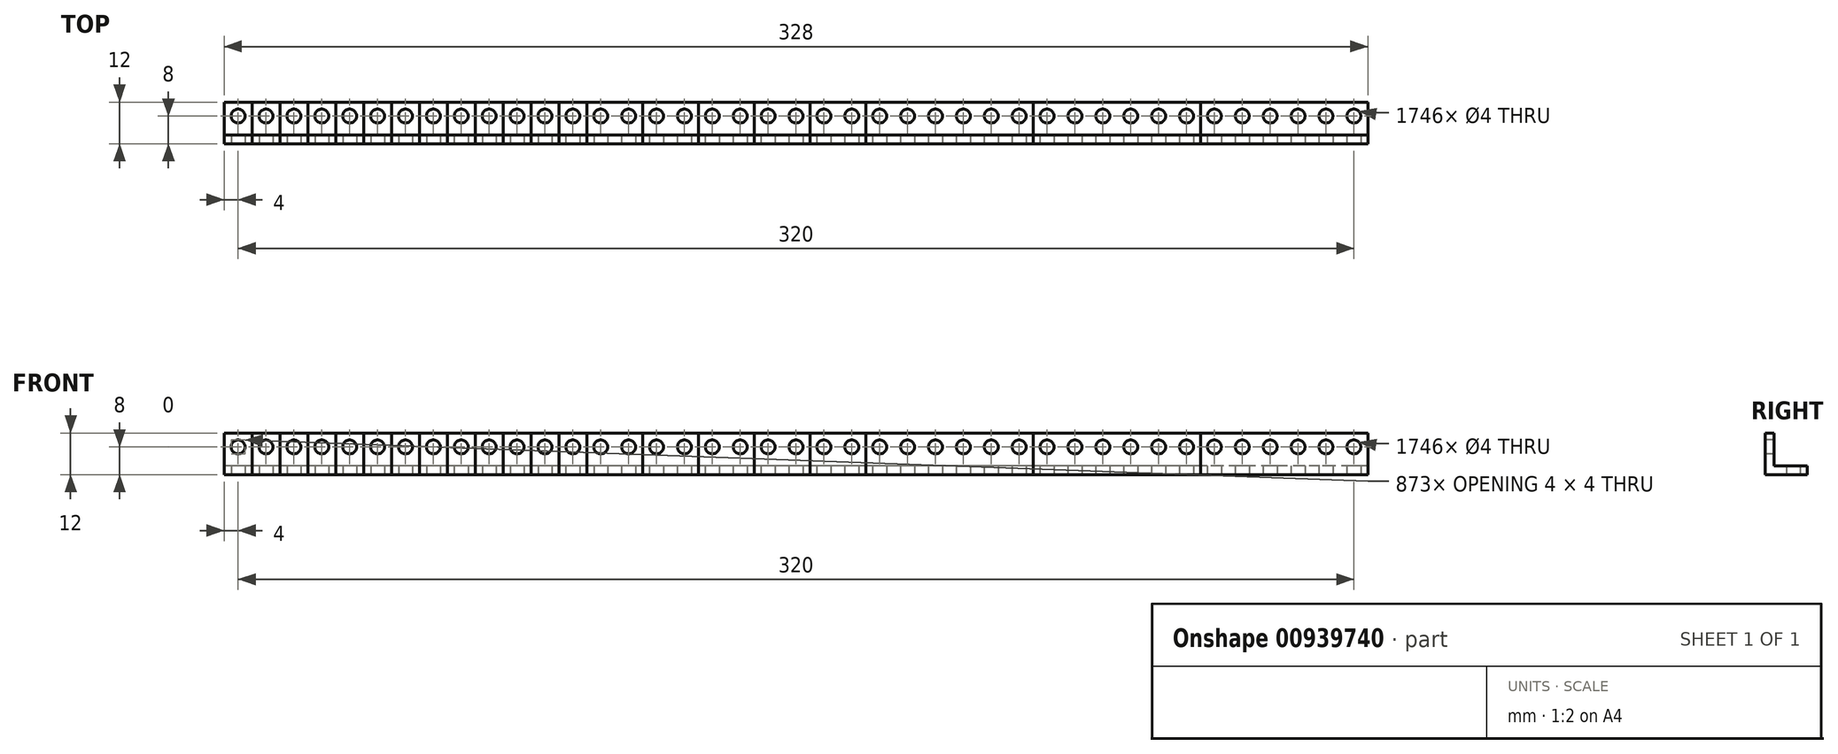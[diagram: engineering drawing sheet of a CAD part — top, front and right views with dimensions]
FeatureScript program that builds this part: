
annotation { "Feature Type Name" : "Feature", "Feature Type Description" : "" }
export const myFeature = defineFeature(function(context is Context, id is Id, definition is map)
    precondition{}
    {
        {
            var Q0;
            Q0=qCreatedBy(makeId("Right.planeOp"),FACE);
            var sketch = newSketch(context, id + "F0", { "sketchPlane" : qUnion([Q0])});
            skLineSegment(sketch, "E0.bottom", {"start": v(0, 0) * mm, "end": v(12, 0) * mm});
            skLineSegment(sketch, "E0.top", {"start": v(0, 12) * mm, "end": v(2.5, 12) * mm});
            skLineSegment(sketch, "E0.left", {"start": v(0, 0) * mm, "end": v(0, 12) * mm});
            skLineSegment(sketch, "E1.left", {"start": v(2.5, 12) * mm, "end": v(2.5, 2.5) * mm});
            skLineSegment(sketch, "E2", {"start": v(12, 0) * mm, "end": v(12, 2.5) * mm});
            skLineSegment(sketch, "E3", {"start": v(2.5, 2.5) * mm, "end": v(12, 2.5) * mm});
            skSolve(sketch);
        }
        {
            var Q0;
            Q0=qSketchRegion(id+"F0",true);
            extrude(context, id + "F1", {"entities" : qUnion([Q0]), "depth" : 8 * mm, "offsetDistance" : 25 * mm});
        }
        {
            var Q0;
            Q0=qSketchRegion(id+"F0",true);
            extrude(context, id + "F2", {"entities" : qUnion([Q0]), "depth" : 16 * mm, "offsetDistance" : 25 * mm});
        }
        {
            var Q0;
            Q0=qSketchRegion(id+"F0",true);
            extrude(context, id + "F3", {"entities" : qUnion([Q0]), "depth" : 24 * mm, "offsetDistance" : 25 * mm});
        }
        {
            var Q0;
            Q0=qSketchRegion(id+"F0",true);
            extrude(context, id + "F4", {"entities" : qUnion([Q0]), "depth" : 32 * mm, "offsetDistance" : 25 * mm});
        }
        {
            var Q0;
            Q0=qSketchRegion(id+"F0",true);
            extrude(context, id + "F5", {"entities" : qUnion([Q0]), "depth" : 40 * mm, "offsetDistance" : 25 * mm});
        }
        {
            var Q0;
            Q0=qSketchRegion(id+"F0",true);
            extrude(context, id + "F6", {"entities" : qUnion([Q0]), "depth" : 48 * mm, "offsetDistance" : 25 * mm});
        }
        {
            var Q0;
            Q0=qSketchRegion(id+"F0",true);
            extrude(context, id + "F7", {"entities" : qUnion([Q0]), "depth" : 56 * mm, "offsetDistance" : 25 * mm});
        }
        {
            var Q0;
            Q0=qSketchRegion(id+"F0",true);
            extrude(context, id + "F8", {"entities" : qUnion([Q0]), "depth" : 64 * mm, "offsetDistance" : 25 * mm});
        }
        {
            var Q0;
            Q0=qSketchRegion(id+"F0",true);
            extrude(context, id + "F9", {"entities" : qUnion([Q0]), "depth" : 72 * mm, "offsetDistance" : 25 * mm});
        }
        {
            var Q0;
            Q0=qSketchRegion(id+"F0",true);
            extrude(context, id + "F10", {"entities" : qUnion([Q0]), "depth" : 80 * mm, "offsetDistance" : 25 * mm});
        }
        {
            var Q0;
            Q0=qSketchRegion(id+"F0",true);
            extrude(context, id + "F11", {"entities" : qUnion([Q0]), "depth" : 88 * mm, "offsetDistance" : 25 * mm});
        }
        {
            var Q0;
            Q0=qSketchRegion(id+"F0",true);
            extrude(context, id + "F12", {"entities" : qUnion([Q0]), "depth" : 96 * mm, "offsetDistance" : 25 * mm});
        }
        {
            var Q0;
            Q0=qSketchRegion(id+"F0",true);
            extrude(context, id + "F13", {"entities" : qUnion([Q0]), "depth" : 104 * mm, "offsetDistance" : 25 * mm});
        }
        {
            var Q0;
            Q0=qSketchRegion(id+"F0",true);
            extrude(context, id + "F14", {"entities" : qUnion([Q0]), "depth" : 120 * mm, "offsetDistance" : 25 * mm});
        }
        {
            var Q0;
            Q0=qSketchRegion(id+"F0",true);
            extrude(context, id + "F15", {"entities" : qUnion([Q0]), "depth" : 136 * mm, "offsetDistance" : 25 * mm});
        }
        {
            var Q0;
            Q0=qSketchRegion(id+"F0",true);
            extrude(context, id + "F16", {"entities" : qUnion([Q0]), "depth" : 152 * mm, "offsetDistance" : 25 * mm});
        }
        {
            var Q0;
            Q0=qSketchRegion(id+"F0",true);
            extrude(context, id + "F17", {"entities" : qUnion([Q0]), "depth" : 168 * mm, "offsetDistance" : 25 * mm});
        }
        {
            var Q0;
            Q0=qSketchRegion(id+"F0",true);
            extrude(context, id + "F18", {"entities" : qUnion([Q0]), "depth" : 184 * mm, "offsetDistance" : 25 * mm});
        }
        {
            var Q0;
            Q0=qSketchRegion(id+"F0",true);
            extrude(context, id + "F19", {"entities" : qUnion([Q0]), "depth" : 232 * mm, "offsetDistance" : 25 * mm});
        }
        {
            var Q0;
            Q0=qSketchRegion(id+"F0",true);
            extrude(context, id + "F20", {"entities" : qUnion([Q0]), "depth" : 280 * mm, "offsetDistance" : 25 * mm});
        }
        {
            var Q0;
            Q0=qSketchRegion(id+"F0",true);
            extrude(context, id + "F21", {"entities" : qUnion([Q0]), "depth" : 328 * mm, "offsetDistance" : 25 * mm});
        }
        {
            var Q0;
            Q0=qCreatedBy(makeId("Front.planeOp"),FACE);
            var sketch = newSketch(context, id + "F22", { "sketchPlane" : qUnion([Q0])});
            skLineSegment(sketch, "E4.bottom", {"start": v(0, 0) * mm, "end": v(4, 0) * mm, "construction": true});
            skLineSegment(sketch, "E4.top", {"start": v(0, 8) * mm, "end": v(4, 8) * mm, "construction": true});
            skLineSegment(sketch, "E4.left", {"start": v(0, 0) * mm, "end": v(0, 8) * mm, "construction": true});
            skLineSegment(sketch, "E4.right", {"start": v(4, 0) * mm, "end": v(4, 8) * mm, "construction": true});
            skCircle(sketch, "E5", {"center": v(4, 8) * mm, "radius": 2 * mm});
            skCircle(sketch, "E6.1.0.0", {"center": v(12, 8) * mm, "radius": 2 * mm});
            skCircle(sketch, "E6.2.0.0", {"center": v(20, 8) * mm, "radius": 2 * mm});
            skLineSegment(sketch, "E6.direction1", {"start": v(4, 8) * mm, "end": v(12, 8) * mm, "construction": true});
            skCircle(sketch, "E7.0.3.0", {"center": v(28, 8) * mm, "radius": 2 * mm});
            skCircle(sketch, "E7.0.4.0", {"center": v(36, 8) * mm, "radius": 2 * mm});
            skCircle(sketch, "E7.0.5.0", {"center": v(44, 8) * mm, "radius": 2 * mm});
            skCircle(sketch, "E7.0.6.0", {"center": v(52, 8) * mm, "radius": 2 * mm});
            skCircle(sketch, "E7.0.7.0", {"center": v(60, 8) * mm, "radius": 2 * mm});
            skCircle(sketch, "E7.0.8.0", {"center": v(68, 8) * mm, "radius": 2 * mm});
            skCircle(sketch, "E7.0.9.0", {"center": v(76, 8) * mm, "radius": 2 * mm});
            skCircle(sketch, "E7.0.10.0", {"center": v(84, 8) * mm, "radius": 2 * mm});
            skCircle(sketch, "E7.0.11.0", {"center": v(92, 8) * mm, "radius": 2 * mm});
            skCircle(sketch, "E7.0.12.0", {"center": v(100, 8) * mm, "radius": 2 * mm});
            skCircle(sketch, "E7.0.13.0", {"center": v(108, 8) * mm, "radius": 2 * mm});
            skCircle(sketch, "E7.0.14.0", {"center": v(116, 8) * mm, "radius": 2 * mm});
            skCircle(sketch, "E7.0.15.0", {"center": v(124, 8) * mm, "radius": 2 * mm});
            skCircle(sketch, "E7.0.16.0", {"center": v(132, 8) * mm, "radius": 2 * mm});
            skCircle(sketch, "E7.0.17.0", {"center": v(140, 8) * mm, "radius": 2 * mm});
            skCircle(sketch, "E7.0.18.0", {"center": v(148, 8) * mm, "radius": 2 * mm});
            skCircle(sketch, "E7.0.19.0", {"center": v(156, 8) * mm, "radius": 2 * mm});
            skCircle(sketch, "E7.0.20.0", {"center": v(164, 8) * mm, "radius": 2 * mm});
            skCircle(sketch, "E7.0.21.0", {"center": v(172, 8) * mm, "radius": 2 * mm});
            skCircle(sketch, "E7.0.22.0", {"center": v(180, 8) * mm, "radius": 2 * mm});
            skCircle(sketch, "E7.0.23.0", {"center": v(188, 8) * mm, "radius": 2 * mm});
            skCircle(sketch, "E7.0.24.0", {"center": v(196, 8) * mm, "radius": 2 * mm});
            skCircle(sketch, "E7.0.25.0", {"center": v(204, 8) * mm, "radius": 2 * mm});
            skCircle(sketch, "E7.0.26.0", {"center": v(212, 8) * mm, "radius": 2 * mm});
            skCircle(sketch, "E7.0.27.0", {"center": v(220, 8) * mm, "radius": 2 * mm});
            skCircle(sketch, "E7.0.28.0", {"center": v(228, 8) * mm, "radius": 2 * mm});
            skCircle(sketch, "E7.0.29.0", {"center": v(236, 8) * mm, "radius": 2 * mm});
            skCircle(sketch, "E7.0.30.0", {"center": v(244, 8) * mm, "radius": 2 * mm});
            skCircle(sketch, "E7.0.31.0", {"center": v(252, 8) * mm, "radius": 2 * mm});
            skCircle(sketch, "E7.0.32.0", {"center": v(260, 8) * mm, "radius": 2 * mm});
            skCircle(sketch, "E7.0.33.0", {"center": v(268, 8) * mm, "radius": 2 * mm});
            skCircle(sketch, "E7.0.34.0", {"center": v(276, 8) * mm, "radius": 2 * mm});
            skCircle(sketch, "E7.0.35.0", {"center": v(284, 8) * mm, "radius": 2 * mm});
            skCircle(sketch, "E7.0.36.0", {"center": v(292, 8) * mm, "radius": 2 * mm});
            skCircle(sketch, "E7.0.37.0", {"center": v(300, 8) * mm, "radius": 2 * mm});
            skCircle(sketch, "E7.0.38.0", {"center": v(308, 8) * mm, "radius": 2 * mm});
            skCircle(sketch, "E7.0.39.0", {"center": v(316, 8) * mm, "radius": 2 * mm});
            skCircle(sketch, "E7.0.40.0", {"center": v(324, 8) * mm, "radius": 2 * mm});
            skSolve(sketch);
        }
        {
            var Q0;
            Q0=qSketchRegion(id+"F22",true);
            extrude(context, id + "F23", {"entities" : qUnion([Q0]), "operationType" : NewBodyOperationType.REMOVE, "endBound" : BoundingType.THROUGH_ALL, "oppositeDirection" : true, "depth" : 25 * mm, "offsetDistance" : 25 * mm});
        }
        {
            var Q0;
            Q0=qCreatedBy(makeId("Top.planeOp"),FACE);
            var sketch = newSketch(context, id + "F24", { "sketchPlane" : qUnion([Q0])});
            skPoint(sketch, "E8.0", {"position": v(0, 12) * mm});
            skLineSegment(sketch, "E9.top", {"start": v(0, 0) * mm, "end": v(4, 0) * mm, "construction": true});
            skLineSegment(sketch, "E9.right", {"start": v(4, 8) * mm, "end": v(4, 0) * mm, "construction": true});
            skCircle(sketch, "E10", {"center": v(4, 8) * mm, "radius": 2 * mm});
            skCircle(sketch, "E11.1.0.0", {"center": v(12, 8) * mm, "radius": 2 * mm});
            skCircle(sketch, "E11.2.0.0", {"center": v(20, 8) * mm, "radius": 2 * mm});
            skCircle(sketch, "E11.3.0.0", {"center": v(28, 8) * mm, "radius": 2 * mm});
            skCircle(sketch, "E11.4.0.0", {"center": v(36, 8) * mm, "radius": 2 * mm});
            skCircle(sketch, "E11.5.0.0", {"center": v(44, 8) * mm, "radius": 2 * mm});
            skCircle(sketch, "E11.6.0.0", {"center": v(52, 8) * mm, "radius": 2 * mm});
            skCircle(sketch, "E11.7.0.0", {"center": v(60, 8) * mm, "radius": 2 * mm});
            skCircle(sketch, "E11.8.0.0", {"center": v(68, 8) * mm, "radius": 2 * mm});
            skCircle(sketch, "E11.9.0.0", {"center": v(76, 8) * mm, "radius": 2 * mm});
            skCircle(sketch, "E11.10.0.0", {"center": v(84, 8) * mm, "radius": 2 * mm});
            skCircle(sketch, "E11.11.0.0", {"center": v(92, 8) * mm, "radius": 2 * mm});
            skCircle(sketch, "E11.12.0.0", {"center": v(100, 8) * mm, "radius": 2 * mm});
            skCircle(sketch, "E11.13.0.0", {"center": v(108, 8) * mm, "radius": 2 * mm});
            skCircle(sketch, "E11.14.0.0", {"center": v(116, 8) * mm, "radius": 2 * mm});
            skCircle(sketch, "E11.15.0.0", {"center": v(124, 8) * mm, "radius": 2 * mm});
            skCircle(sketch, "E11.16.0.0", {"center": v(132, 8) * mm, "radius": 2 * mm});
            skCircle(sketch, "E11.17.0.0", {"center": v(140, 8) * mm, "radius": 2 * mm});
            skCircle(sketch, "E11.18.0.0", {"center": v(148, 8) * mm, "radius": 2 * mm});
            skCircle(sketch, "E11.19.0.0", {"center": v(156, 8) * mm, "radius": 2 * mm});
            skCircle(sketch, "E11.20.0.0", {"center": v(164, 8) * mm, "radius": 2 * mm});
            skCircle(sketch, "E11.21.0.0", {"center": v(172, 8) * mm, "radius": 2 * mm});
            skCircle(sketch, "E11.22.0.0", {"center": v(180, 8) * mm, "radius": 2 * mm});
            skCircle(sketch, "E11.23.0.0", {"center": v(188, 8) * mm, "radius": 2 * mm});
            skCircle(sketch, "E11.24.0.0", {"center": v(196, 8) * mm, "radius": 2 * mm});
            skCircle(sketch, "E11.25.0.0", {"center": v(204, 8) * mm, "radius": 2 * mm});
            skCircle(sketch, "E11.26.0.0", {"center": v(212, 8) * mm, "radius": 2 * mm});
            skCircle(sketch, "E11.27.0.0", {"center": v(220, 8) * mm, "radius": 2 * mm});
            skCircle(sketch, "E11.28.0.0", {"center": v(228, 8) * mm, "radius": 2 * mm});
            skCircle(sketch, "E11.29.0.0", {"center": v(236, 8) * mm, "radius": 2 * mm});
            skCircle(sketch, "E11.30.0.0", {"center": v(244, 8) * mm, "radius": 2 * mm});
            skCircle(sketch, "E11.31.0.0", {"center": v(252, 8) * mm, "radius": 2 * mm});
            skCircle(sketch, "E11.32.0.0", {"center": v(260, 8) * mm, "radius": 2 * mm});
            skCircle(sketch, "E11.33.0.0", {"center": v(268, 8) * mm, "radius": 2 * mm});
            skCircle(sketch, "E11.34.0.0", {"center": v(276, 8) * mm, "radius": 2 * mm});
            skCircle(sketch, "E11.35.0.0", {"center": v(284, 8) * mm, "radius": 2 * mm});
            skCircle(sketch, "E11.36.0.0", {"center": v(292, 8) * mm, "radius": 2 * mm});
            skCircle(sketch, "E11.37.0.0", {"center": v(300, 8) * mm, "radius": 2 * mm});
            skCircle(sketch, "E11.38.0.0", {"center": v(308, 8) * mm, "radius": 2 * mm});
            skCircle(sketch, "E11.39.0.0", {"center": v(316, 8) * mm, "radius": 2 * mm});
            skCircle(sketch, "E11.40.0.0", {"center": v(324, 8) * mm, "radius": 2 * mm});
            skLineSegment(sketch, "E11.direction1", {"start": v(4, 8) * mm, "end": v(12, 8) * mm, "construction": true});
            skPoint(sketch, "E12.orphan", {"position": v(4, 16) * mm});
            skSolve(sketch);
        }
        {
            var Q0;
            Q0=qSketchRegion(id+"F24",true);
            extrude(context, id + "F25", {"entities" : qUnion([Q0]), "operationType" : NewBodyOperationType.REMOVE, "endBound" : BoundingType.THROUGH_ALL, "depth" : 25 * mm, "offsetDistance" : 25 * mm});
        }
    });
